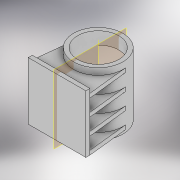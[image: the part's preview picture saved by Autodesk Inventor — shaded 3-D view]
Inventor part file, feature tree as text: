
AUTODESK INVENTOR PART (.ipt)
format: ipt  version: 2017 (Build 210142000, 142)  size: 178,688 bytes
history: native  units: mm
features: extrude x3, plane x2, sketch x2, pattern_linear x1, other x1, revolve x1
ambient origin geometry x8: Origin, YZ Plane, XZ Plane, XY Plane, X Axis, Y Axis, Z Axis, Center Point
bodies: Solid1 (feature_tree)
feature tree (10):
  extrude  "Extrusion1"  Depth=70.0mm
  plane  "Work Plane2"
  extrude  "Extrusion2"  Depth=50.0mm
  pattern_linear  "Rectangular Pattern1"  Count1=5  [1 undecoded]
  extrude  "Extrusion3"  Depth=60.0mm
  plane  "Work Plane1"
  sketch  "Sketch3"  dims[d2=5.0mm d3=0.0mm d4=50.0mm d5=50.0mm d6=60.0mm d7=5.0mm d8=0.0mm d9=50.0mm d11=15.0mm d12=70.0mm d13=73.0mm d14=0.0mm d15=0.0mm d18=90.0deg d19=15.0mm d20=15.0mm]
  other  "Work Axis1"
  revolve  "Revolution1"  [1 undecoded]
  sketch  "Sketch1"  dims[d0=70.0mm d1=70.0mm]
note: 2 required parameter values undecoded (feature->parameter linkage not recoverable at this tier; creation-order binding heuristic only, values carry confidence <= 0.55)